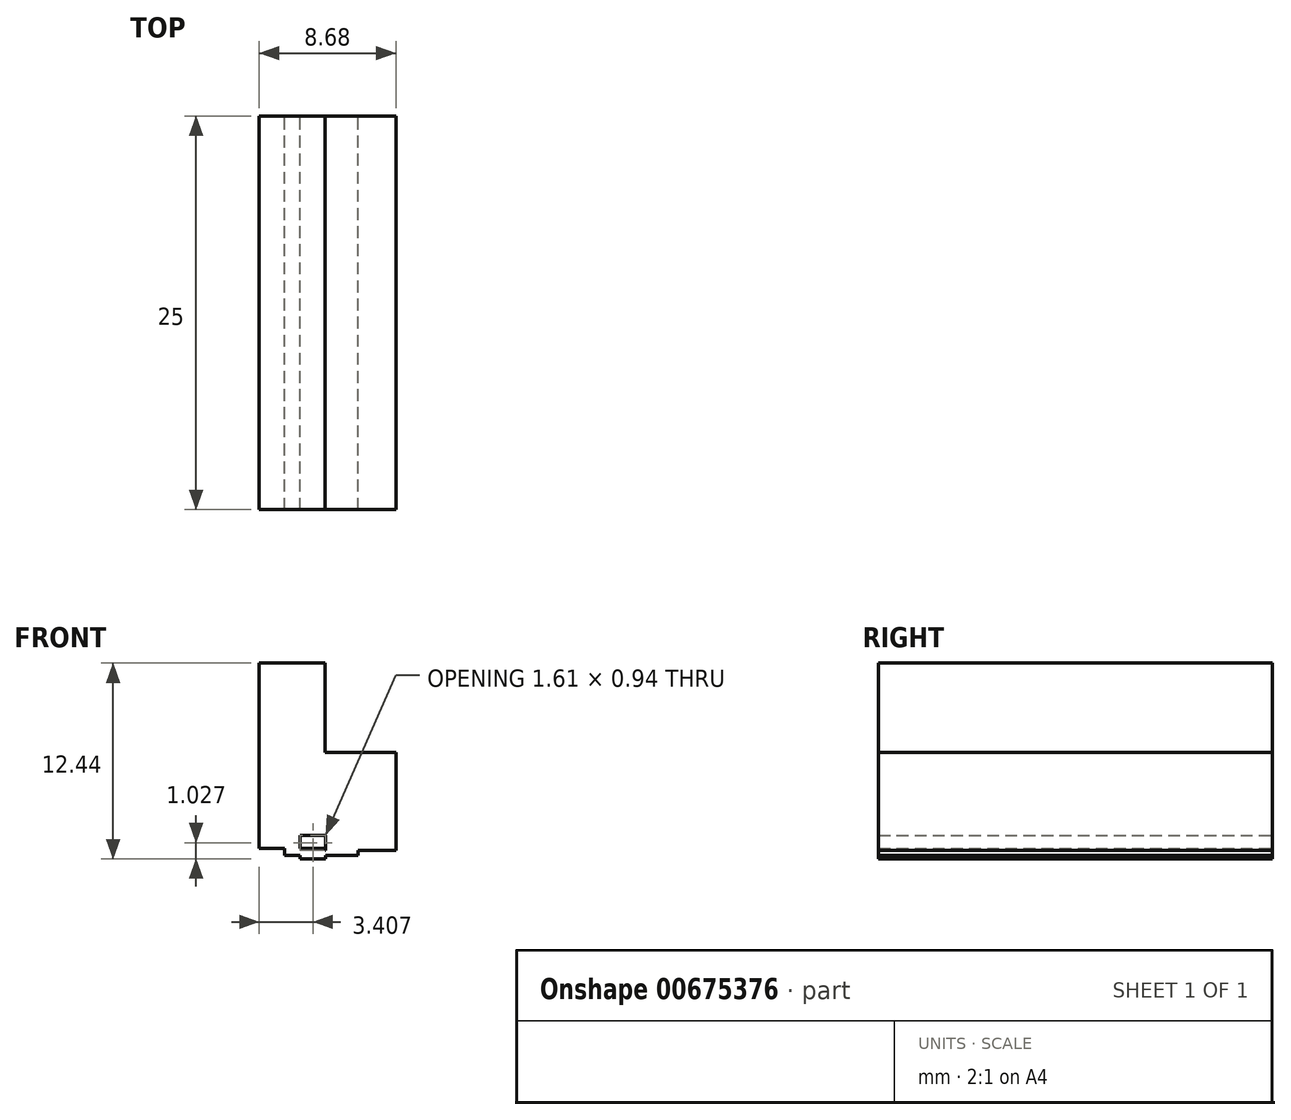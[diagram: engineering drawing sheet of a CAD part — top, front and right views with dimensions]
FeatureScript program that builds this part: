
annotation { "Feature Type Name" : "Feature", "Feature Type Description" : "" }
export const myFeature = defineFeature(function(context is Context, id is Id, definition is map)
    precondition{}
    {
        {
            var Q0;
            Q0=qCreatedBy(makeId("Front.planeOp"),FACE);
            var sketch = newSketch(context, id + "F0", { "sketchPlane" : qUnion([Q0])});
            skLineSegment(sketch, "E0.bottom", {"start": v(-13.7, 23.25) * mm, "end": v(-9.52, 23.25) * mm});
            skLineSegment(sketch, "E0.top", {"start": v(-13.7, 11.48) * mm, "end": v(-9.52, 11.48) * mm});
            skLineSegment(sketch, "E0.left", {"start": v(-13.7, 23.25) * mm, "end": v(-13.7, 11.48) * mm});
            skLineSegment(sketch, "E0.right", {"start": v(-9.52, 23.25) * mm, "end": v(-9.52, 11.48) * mm});
            skLineSegment(sketch, "E1.bottom", {"start": v(-9.52, 11.37) * mm, "end": v(-5.02, 11.37) * mm});
            skLineSegment(sketch, "E1.top", {"start": v(-9.52, 17.57) * mm, "end": v(-5.02, 17.57) * mm});
            skLineSegment(sketch, "E1.left", {"start": v(-9.52, 11.37) * mm, "end": v(-9.52, 17.57) * mm});
            skLineSegment(sketch, "E1.right", {"start": v(-5.02, 11.37) * mm, "end": v(-5.02, 17.57) * mm});
            skLineSegment(sketch, "E2.bottom", {"start": v(-7.43, 15.26) * mm, "end": v(-12.09, 15.26) * mm});
            skLineSegment(sketch, "E2.top", {"start": v(-7.43, 11.03) * mm, "end": v(-12.09, 11.03) * mm});
            skLineSegment(sketch, "E2.left", {"start": v(-7.43, 15.26) * mm, "end": v(-7.43, 11.03) * mm});
            skLineSegment(sketch, "E2.right", {"start": v(-12.09, 15.26) * mm, "end": v(-12.09, 11.03) * mm});
            skLineSegment(sketch, "E3.bottom", {"start": v(-11.1, 10.81) * mm, "end": v(-9.49, 10.81) * mm});
            skLineSegment(sketch, "E3.top", {"start": v(-11.1, 12.3) * mm, "end": v(-9.49, 12.3) * mm});
            skLineSegment(sketch, "E3.left", {"start": v(-11.1, 10.81) * mm, "end": v(-11.1, 12.3) * mm});
            skLineSegment(sketch, "E3.right", {"start": v(-9.49, 10.81) * mm, "end": v(-9.49, 12.3) * mm});
            skSolve(sketch);
        }
        {
            var Q0;
            {var subQ1=sQuery(id+"F0.wireOp",EDGE,"E1.top");Q0=makeQuery(id+"F0.imprint","IMPRINT",FACE,{"disambiguationData":[TD([[makeQuery(id+"F0.imprint","IMPRINT",EDGE,{"derivedFrom":subQ1}),-1.0]])]});}
            var Q1;
            Q1 = qSketchRegion(id + "F0", true);
            extrude(context, id + "F1", {"entities" : qUnion([Q0, Q1]), "depth" : 25 * mm, "offsetDistance" : 25 * mm});
        }
    });
